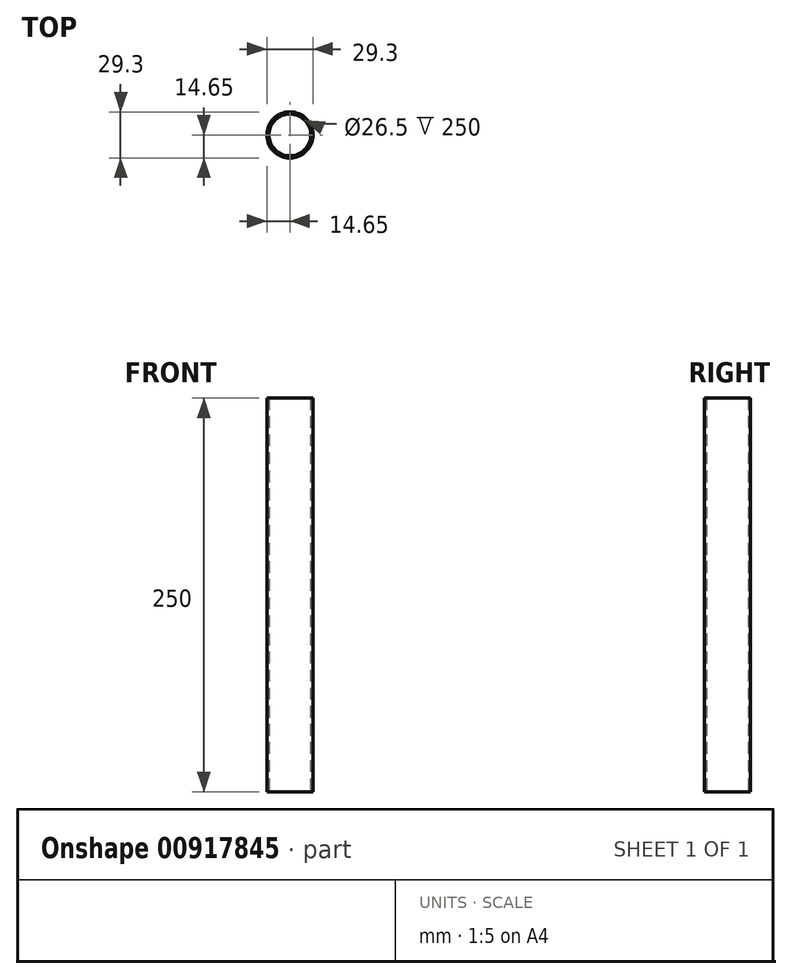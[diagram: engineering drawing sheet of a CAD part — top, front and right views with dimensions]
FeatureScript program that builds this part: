
annotation { "Feature Type Name" : "Feature", "Feature Type Description" : "" }
export const myFeature = defineFeature(function(context is Context, id is Id, definition is map)
    precondition{}
    {
        {
            var Q0;
            Q0=qCreatedBy(makeId("Top.planeOp"),FACE);
            var sketch = newSketch(context, id + "F0", { "sketchPlane" : qUnion([Q0])});
            skCircle(sketch, "E0", {"center": v(0, 0) * mm, "radius": 14.65 * mm});
            skCircle(sketch, "E1", {"center": v(0, 0) * mm, "radius": 13.25 * mm});
            skSolve(sketch);
        }
        {
            var Q0;
            Q0=makeQuery(id+"F0.imprint","IMPRINT",FACE,{"disambiguationData":[TD([[makeQuery(id+"F0.imprint","IMPRINT",EDGE,{"derivedFrom":sQuery(id+"F0.wireOp",EDGE,"E0")}),1.0]])]});
            extrude(context, id + "F1", {"entities" : qUnion([Q0]), "depth" : 250 * mm, "offsetDistance" : 25 * mm});
        }
    });
